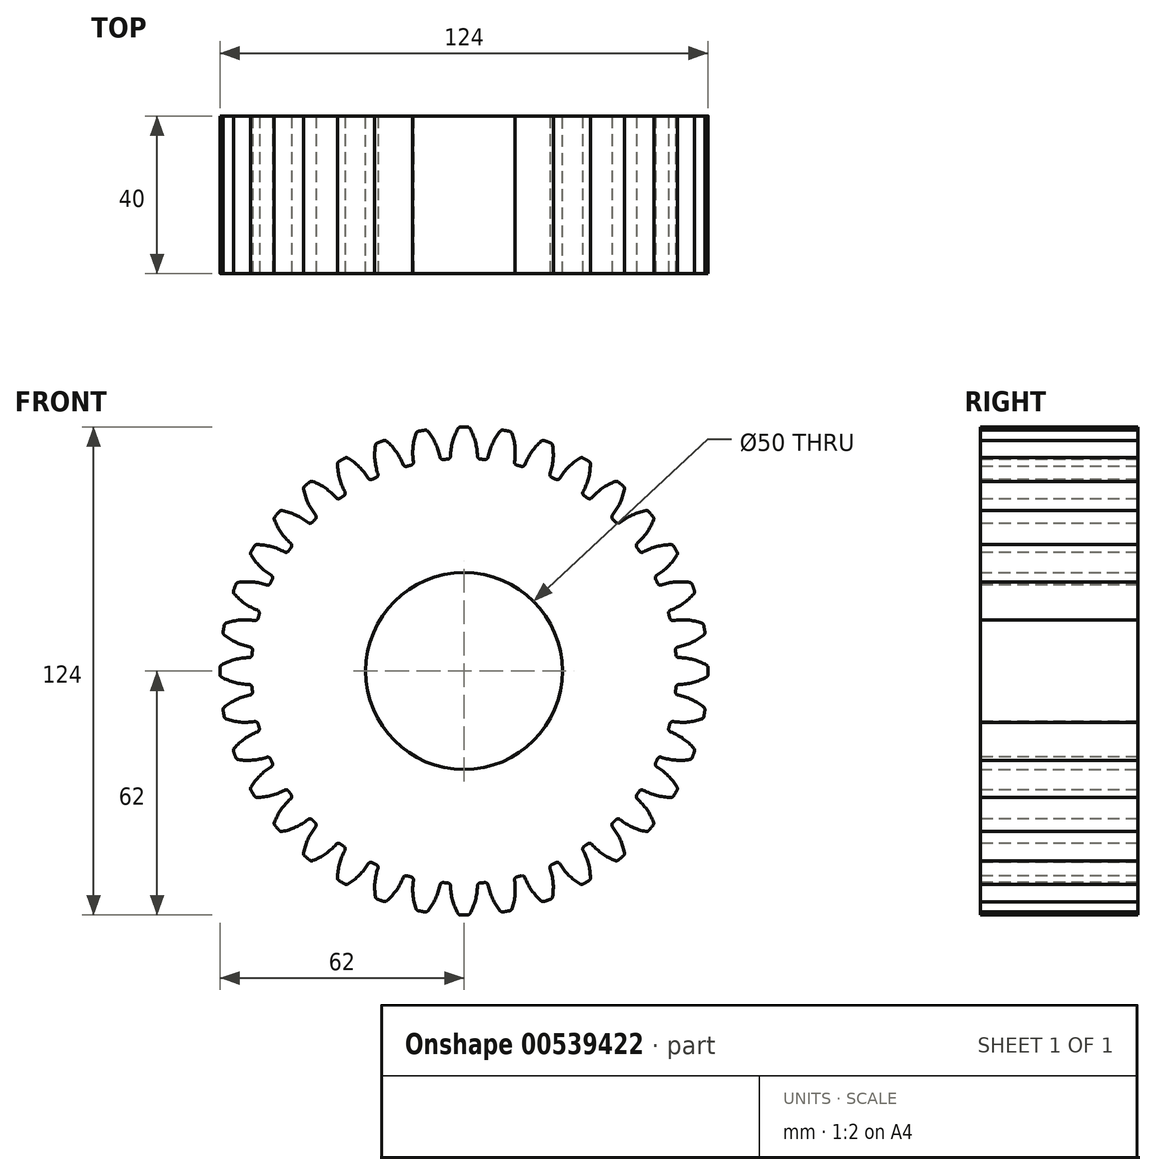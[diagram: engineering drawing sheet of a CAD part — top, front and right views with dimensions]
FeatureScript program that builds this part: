
annotation { "Feature Type Name" : "Feature", "Feature Type Description" : "" }
export const myFeature = defineFeature(function(context is Context, id is Id, definition is map)
    precondition{}
    {
        {
            var Q0;
            Q0=qCreatedBy(makeId("Front.planeOp"),FACE);
            var sketch = newSketch(context, id + "F0", { "sketchPlane" : qUnion([Q0])});
            skArc(sketch, "E0", {"start": v(2.18, 24.9) * mm, "mid": v(0, 25) * mm, "end": v(-2.18, 24.9) * mm});
            skLineSegment(sketch, "E1", {"start": v(0, 0) * mm, "end": v(0, 60) * mm, "construction": true});
            skArc(sketch, "E2", {"start": v(4.7, 53.8) * mm, "mid": v(4.06, 53.85) * mm, "end": v(3.4, 53.9) * mm});
            skLineSegment(sketch, "E3", {"start": v(2.18, 24.9) * mm, "end": v(4.7, 53.8) * mm});
            skLineSegment(sketch, "E4", {"start": v(-2.18, 24.9) * mm, "end": v(-4.7, 53.8) * mm});
            skArc(sketch, "E5", {"start": v(-1.3, 61.99) * mm, "mid": v(-2.93, 58.09) * mm, "end": v(-3.4, 53.9) * mm});
            skArc(sketch, "E6.MirrorCS", {"start": v(1.3, 61.99) * mm, "mid": v(2.93, 58.09) * mm, "end": v(3.4, 53.9) * mm});
            skArc(sketch, "E7.trimOffspring", {"start": v(1.3, 61.99) * mm, "mid": v(0, 62) * mm, "end": v(-1.3, 61.99) * mm});
            skArc(sketch, "E8.trimOffspring", {"start": v(-3.4, 53.9) * mm, "mid": v(-4.06, 53.85) * mm, "end": v(-4.7, 53.8) * mm});
            skSolve(sketch);
        }
        {
            var Q0;
            Q0 = qSketchRegion(id + "F0", true);
            extrude(context, id + "F1", {"entities" : qUnion([Q0]), "depth" : 40 * mm, "offsetDistance" : 25 * mm});
        }
        {
            var Q0;
            Q0=makeQuery(id+"F1.opExtrude","SWEPT_EDGE",EDGE,{"disambiguationData":[OSD([sQuery(id+"F0.wireOp",EDGE,"E5"),sQuery(id+"F0.wireOp",EDGE,"E8.trimOffspring")])]});
            var Q1;
            Q1=makeQuery(id+"F1.opExtrude","SWEPT_EDGE",EDGE,{"disambiguationData":[OSD([sQuery(id+"F0.wireOp",EDGE,"E5"),sQuery(id+"F0.wireOp",EDGE,"E7.trimOffspring")])]});
            var Q2;
            Q2=makeQuery(id+"F1.opExtrude","SWEPT_EDGE",EDGE,{"disambiguationData":[OSD([sQuery(id+"F0.wireOp",EDGE,"E6.MirrorCS"),sQuery(id+"F0.wireOp",EDGE,"E7.trimOffspring")])]});
            var Q3;
            Q3=makeQuery(id+"F1.opExtrude","SWEPT_EDGE",EDGE,{"disambiguationData":[OSD([sQuery(id+"F0.wireOp",EDGE,"E2"),sQuery(id+"F0.wireOp",EDGE,"E6.MirrorCS")])]});
            fillet(context, id + "F2", {"entities" : qUnion([Q0, Q1, Q2, Q3]), "radius" : 0.8 * mm, "tangentPropagation" : true, "allowEdgeOverflow" : false});
        }
        {
            var Q0;
            Q0=makeQuery(id+"F1.opExtrude","SWEPT_BODY",BODY,{"disambiguationData":[OSD([sQuery(id+"F0.wireOp",EDGE,"E0"),sQuery(id+"F0.wireOp",EDGE,"E2"),sQuery(id+"F0.wireOp",EDGE,"E3"),sQuery(id+"F0.wireOp",EDGE,"E4"),sQuery(id+"F0.wireOp",EDGE,"E5"),sQuery(id+"F0.wireOp",EDGE,"E6.MirrorCS"),sQuery(id+"F0.wireOp",EDGE,"E7.trimOffspring"),sQuery(id+"F0.wireOp",EDGE,"E8.trimOffspring")])]});
            var Q1;
            Q1=makeQuery(id+"F1.opExtrude","SWEPT_FACE",FACE,{"disambiguationData":[OSD([sQuery(id+"F0.wireOp",EDGE,"E0")])]});
            circularPattern(context, id + "F3", {"operationType" : NewBodyOperationType.ADD, "entities" : qUnion([Q0]), "axis" : qUnion([Q1]), "angle" : 360 * degree, "instanceCount" : 36, "equalSpace" : true});
        }
    });
